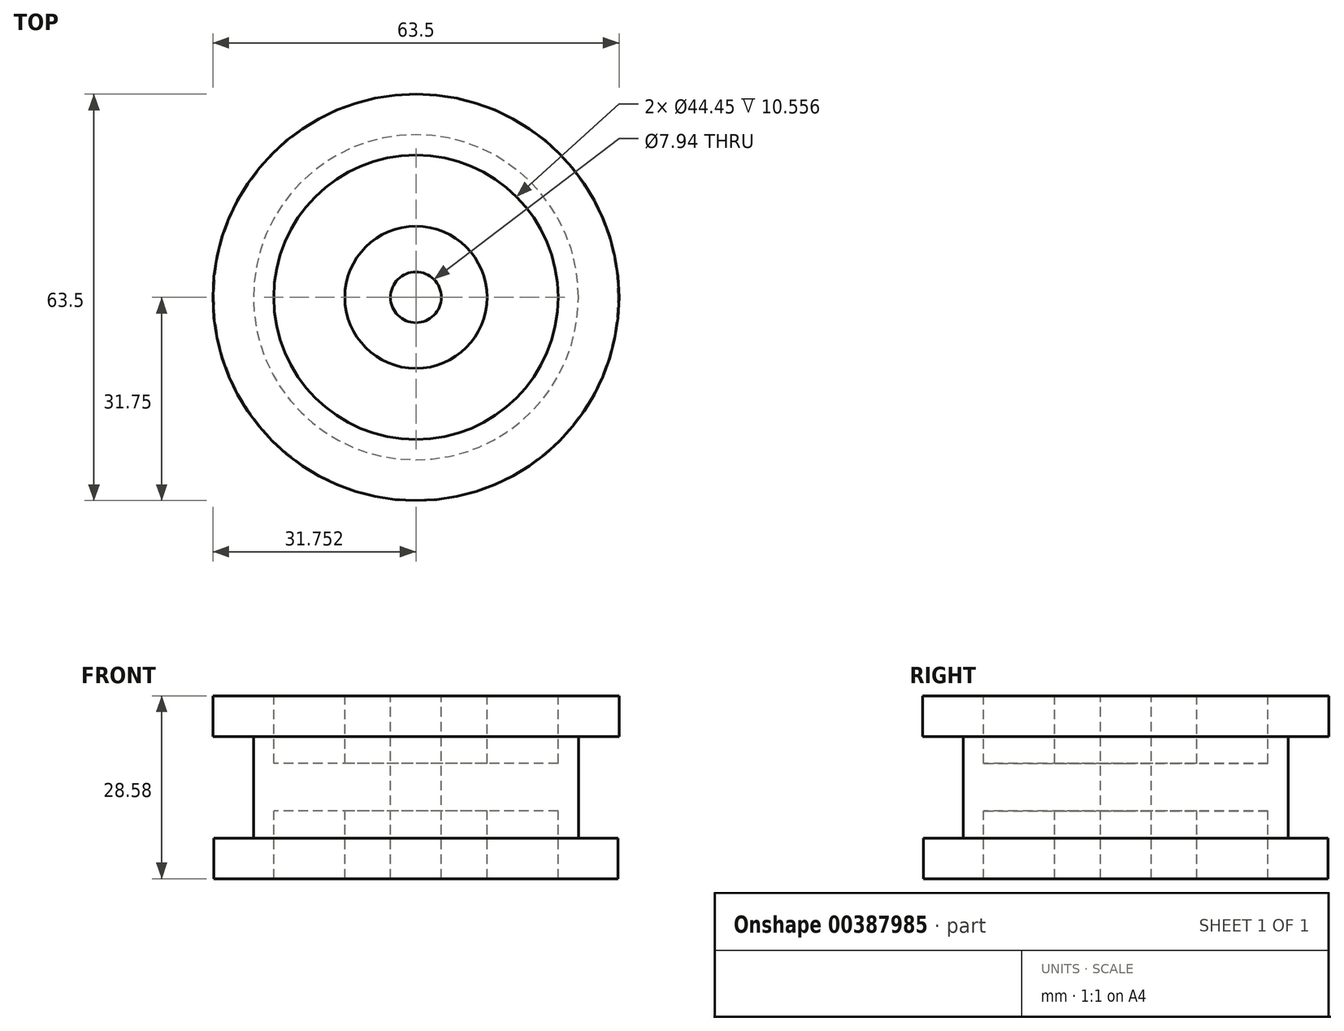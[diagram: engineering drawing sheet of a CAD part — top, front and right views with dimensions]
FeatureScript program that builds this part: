
annotation { "Feature Type Name" : "Feature", "Feature Type Description" : "" }
export const myFeature = defineFeature(function(context is Context, id is Id, definition is map)
    precondition{}
    {
        {
            var Q0;
            Q0=qCreatedBy(makeId("Front.planeOp"),FACE);
            var sketch = newSketch(context, id + "F0", { "sketchPlane" : qUnion([Q0])});
            skLineSegment(sketch, "E0.bottom", {"start": v(-18.15, 17.62) * mm, "end": v(-21.33, 17.62) * mm});
            skLineSegment(sketch, "E0.top", {"start": v(-18.15, -10.96) * mm, "end": v(-21.33, -10.96) * mm});
            skLineSegment(sketch, "E0.right", {"start": v(-21.33, 17.62) * mm, "end": v(-21.33, -10.96) * mm});
            skLineSegment(sketch, "E1.bottom", {"start": v(-21.33, 17.62) * mm, "end": v(-27.68, 17.62) * mm});
            skLineSegment(sketch, "E1.top", {"start": v(-21.33, 11.27) * mm, "end": v(-27.68, 11.27) * mm});
            skLineSegment(sketch, "E1.left", {"start": v(-21.33, 17.62) * mm, "end": v(-21.33, 11.27) * mm});
            skLineSegment(sketch, "E1.right", {"start": v(-27.68, 17.62) * mm, "end": v(-27.68, 11.27) * mm});
            skLineSegment(sketch, "E2.bottom", {"start": v(-21.33, -10.96) * mm, "end": v(-27.54, -10.96) * mm});
            skLineSegment(sketch, "E2.top", {"start": v(-21.33, -4.6) * mm, "end": v(-27.54, -4.6) * mm});
            skLineSegment(sketch, "E2.left", {"start": v(-21.33, -10.96) * mm, "end": v(-21.33, -4.6) * mm});
            skLineSegment(sketch, "E2.right", {"start": v(-27.54, -10.96) * mm, "end": v(-27.54, -4.6) * mm});
            skLineSegment(sketch, "E3.bottom", {"start": v(4.07, 17.62) * mm, "end": v(-7.04, 17.62) * mm});
            skLineSegment(sketch, "E3.top", {"start": v(4.07, -10.96) * mm, "end": v(-7.04, -10.96) * mm});
            skLineSegment(sketch, "E3.left", {"start": v(4.07, 17.62) * mm, "end": v(4.07, -10.96) * mm});
            skLineSegment(sketch, "E3.right", {"start": v(-7.04, 17.62) * mm, "end": v(-7.04, -10.96) * mm});
            skLineSegment(sketch, "E4", {"start": v(-18.15, -0.4) * mm, "end": v(-7.04, -0.4) * mm});
            skLineSegment(sketch, "E5", {"start": v(-18.15, 17.62) * mm, "end": v(-18.15, -0.4) * mm});
            skLineSegment(sketch, "E6", {"start": v(-18.15, -10.96) * mm, "end": v(-18.15, 7.06) * mm});
            skLineSegment(sketch, "E7", {"start": v(-18.15, 7.06) * mm, "end": v(-7.04, 7.06) * mm});
            skSolve(sketch);
        }
        {
            var Q0;
            Q0=makeQuery(id+"F0.imprint","IMPRINT",FACE,{"disambiguationData":[TD([[makeQuery(id+"F0.imprint","IMPRINT",EDGE,{"derivedFrom":sQuery(id+"F0.wireOp",EDGE,"E2.bottom")}),-1.0]])]});
            var Q1;
            Q1=makeQuery(id+"F0.imprint","IMPRINT",FACE,{"disambiguationData":[TD([[makeQuery(id+"F0.imprint","IMPRINT",EDGE,{"derivedFrom":sQuery(id+"F0.wireOp",EDGE,"E0.bottom")}),1.0]])]});
            var Q2;
            Q2=makeQuery(id+"F0.imprint","IMPRINT",FACE,{"disambiguationData":[TD([[makeQuery(id+"F0.imprint","IMPRINT",EDGE,{"derivedFrom":sQuery(id+"F0.wireOp",EDGE,"E1.bottom")}),1.0]])]});
            var Q3;
            {var subQ0=sQuery(id+"F0.wireOp",EDGE,"E4");Q3=makeQuery(id+"F0.imprint","IMPRINT",FACE,{"disambiguationData":[TD([[makeQuery(id+"F0.imprint","IMPRINT",EDGE,{"derivedFrom":subQ0}),1.0]])]});}
            var Q4;
            {var subQ1=sQuery(id+"F0.wireOp",EDGE,"E3.bottom");Q4=makeQuery(id+"F0.imprint","IMPRINT",FACE,{"disambiguationData":[TD([[makeQuery(id+"F0.imprint","IMPRINT",EDGE,{"derivedFrom":subQ1}),1.0]])]});}
            var Q5;
            Q5=sQuery(id+"F0.wireOp",EDGE,"E3.left");
            revolve(context, id + "F1", {"entities" : qUnion([Q0, Q1, Q2, Q3, Q4]), "axis" : qUnion([Q5]), "revolveType" : RevolveType.FULL});
        }
        {
            var Q0;
            Q0=makeQuery(id+"F1.opRevolve","SWEPT_FACE",FACE,{"disambiguationData":[OSD([sQuery(id+"F0.wireOp",EDGE,"E3.bottom")])]});
            var sketch = newSketch(context, id + "F2", { "sketchPlane" : qUnion([Q0])});
            skCircle(sketch, "E8", {"center": v(4.07, 0) * mm, "radius": 3.97 * mm});
            skSolve(sketch);
        }
        {
            var Q0;
            Q0=makeQuery(id+"F2.imprint","IMPRINT",FACE,{"disambiguationData":[TD([[makeQuery(id+"F2.imprint","IMPRINT",EDGE,{"derivedFrom":sQuery(id+"F2.wireOp",EDGE,"E8")}),1.0]])]});
            extrude(context, id + "F3", {"entities" : qUnion([Q0]), "operationType" : NewBodyOperationType.REMOVE, "endBound" : BoundingType.THROUGH_ALL, "oppositeDirection" : true, "depth" : 25.4 * mm});
        }
    });
